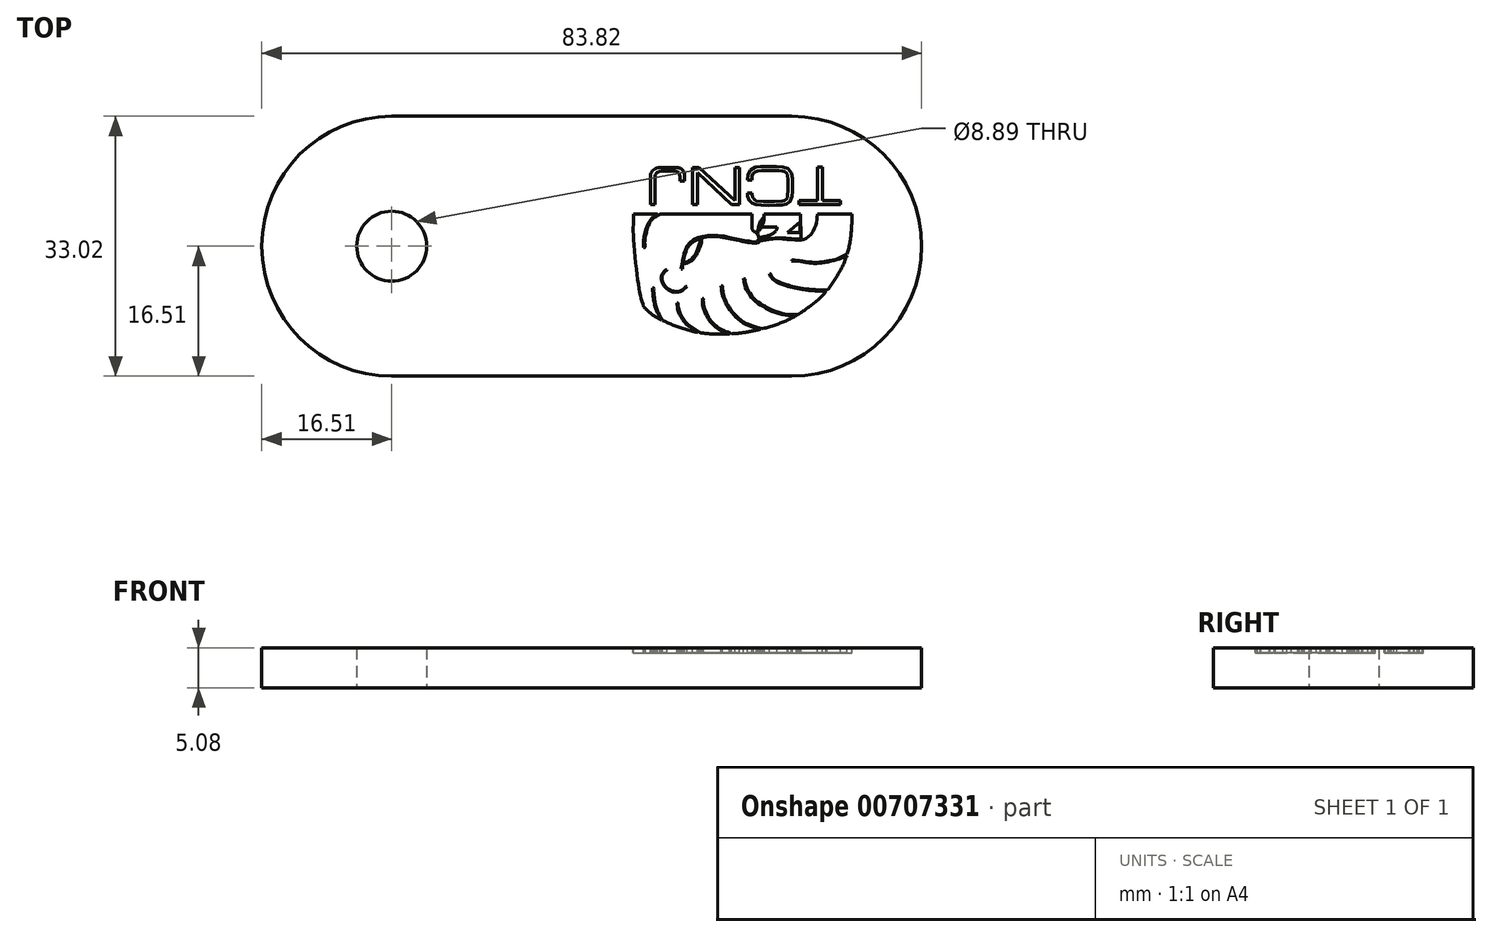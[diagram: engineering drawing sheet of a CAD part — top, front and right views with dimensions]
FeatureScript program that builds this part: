
annotation { "Feature Type Name" : "Feature", "Feature Type Description" : "" }
export const myFeature = defineFeature(function(context is Context, id is Id, definition is map)
    precondition{}
    {
        {
            var Q0;
            Q0=qCreatedBy(makeId("Top.planeOp"),FACE);
            var sketch = newSketch(context, id + "F0", { "sketchPlane" : qUnion([Q0])});
            skLineSegment(sketch, "E0.bottom", {"start": v(0, 0) * mm, "end": v(-50.8, 0) * mm});
            skLineSegment(sketch, "E0.top", {"start": v(0, 33.02) * mm, "end": v(-50.8, 33.02) * mm});
            skArc(sketch, "E1", {"start": v(0, 0) * mm, "mid": v(16.51, 16.51) * mm, "end": v(0, 33.02) * mm});
            skArc(sketch, "E2", {"start": v(-50.8, 33.02) * mm, "mid": v(-67.31, 16.5) * mm, "end": v(-50.8, 0) * mm});
            skCircle(sketch, "E3", {"center": v(-50.8, 16.5) * mm, "radius": 4.45 * mm});
            skSolve(sketch);
        }
        {
            var Q0;
            Q0=makeQuery(id+"F0.imprint","IMPRINT",FACE,{"disambiguationData":[TD([[makeQuery(id+"F0.imprint","IMPRINT",EDGE,{"derivedFrom":sQuery(id+"F0.wireOp",EDGE,"E0.bottom")}),-1.0]])]});
            extrude(context, id + "F1", {"entities" : qUnion([Q0]), "depth" : 5.08 * mm, "offsetDistance" : 25.4 * mm});
        }
        {
            var Q0;
            Q0=makeQuery(id+"F1.opExtrude","CAP_FACE",FACE,{"disambiguationData":[OSD([sQuery(id+"F0.wireOp",EDGE,"E0.bottom"),sQuery(id+"F0.wireOp",EDGE,"E0.top"),sQuery(id+"F0.wireOp",EDGE,"E1"),sQuery(id+"F0.wireOp",EDGE,"E2"),sQuery(id+"F0.wireOp",EDGE,"E3")])],"isStart":false});
            var sketch = newSketch(context, id + "F2", { "sketchPlane" : qUnion([Q0])});
            skLineSegment(sketch, "E4", {"start": v(-20.1, 20.57) * mm, "end": v(7.7, 20.57) * mm});
            skFitSpline(sketch, "E5", {"points": [v(-20.1, 20.57) * mm, v(-20.1, 19.6) * mm, v(-20.1, 17.78) * mm, v(-19.6, 12.72) * mm, v(-19.17, 10.09) * mm, v(-18.79, 8.8) * mm], "startDerivative": vector(0.07, -7.05) * mm, "endDerivative": vector(2.6, -7.75) * mm});
            skFitSpline(sketch, "E6", {"points": [v(-18.79, 8.8) * mm, v(-17.66, 7.8) * mm, v(-16.06, 6.93) * mm, v(-14.16, 6.16) * mm, v(-11.87, 5.55) * mm, v(-9.58, 5.34) * mm, v(-7, 5.42) * mm, v(-4.4, 5.85) * mm, v(-1.6, 6.68) * mm, v(0.61, 7.71) * mm, v(2.2, 8.8) * mm, v(4.02, 10.35) * mm, v(5.62, 12.5) * mm, v(6.75, 14.62) * mm, v(7.44, 17.17) * mm, v(7.7, 20.57) * mm], "startDerivative": vector(19.8, -19.68) * mm, "endDerivative": vector(1.84, 44) * mm});
            skFitSpline(sketch, "E7", {"points": [v(-18.79, 16.33) * mm, v(-18.79, 17.43) * mm, v(-18.52, 18.6) * mm, v(-18.03, 19.74) * mm, v(-17.58, 20.25) * mm, v(-17.3, 20.4) * mm, v(-17.03, 20.57) * mm], "startDerivative": vector(-0.28, 5.46) * mm, "endDerivative": vector(2.48, 1.54) * mm});
            skFitSpline(sketch, "E8", {"points": [v(-15.86, 13.57) * mm, v(-16.17, 13.35) * mm, v(-16.41, 13.03) * mm, v(-16.55, 12.68) * mm, v(-16.53, 12.16) * mm, v(-16.33, 11.62) * mm, v(-15.95, 11.17) * mm, v(-15.56, 10.88) * mm, v(-15.1, 10.67) * mm, v(-14.57, 10.67) * mm, v(-14.03, 10.8) * mm, v(-13.6, 11.1) * mm, v(-13.31, 11.36) * mm], "startDerivative": vector(-4.42, -2.67) * mm, "endDerivative": vector(3.59, 3.47) * mm});
            skFitSpline(sketch, "E9", {"points": [v(-13.88, 13.59) * mm, v(-13.76, 14.6) * mm, v(-13.51, 15.6) * mm, v(-13.15, 16.46) * mm, v(-12.34, 17.17) * mm, v(-11.66, 17.48) * mm, v(-10.7, 17.69) * mm, v(-9.36, 17.7) * mm, v(-8.1, 17.5) * mm, v(-6.87, 17.26) * mm, v(-5.5, 16.98) * mm, v(-4.76, 16.92) * mm, v(-4.16, 17.05) * mm, v(-4, 17.61) * mm, v(-4.26, 18.32) * mm], "startDerivative": vector(1.1, 13.84) * mm, "endDerivative": vector(-5.3, 11.08) * mm});
            skFitSpline(sketch, "E10", {"points": [v(-11.66, 17.48) * mm, v(-11.66, 17) * mm, v(-11.86, 16.36) * mm, v(-12.07, 15.82) * mm, v(-12.34, 15.32) * mm, v(-12.82, 14.8) * mm, v(-13.34, 14.51) * mm, v(-13.79, 14.45) * mm], "startDerivative": vector(0.3, -3.54) * mm, "endDerivative": vector(-3.47, -0.2) * mm});
            skFitSpline(sketch, "E11", {"points": [v(-17.65, 11.2) * mm, v(-17.62, 10.37) * mm, v(-17.45, 9.27) * mm, v(-17.16, 8.36) * mm, v(-16.87, 7.75) * mm, v(-16.53, 7.16) * mm], "startDerivative": vector(0.07, -4.05) * mm, "endDerivative": vector(1.94, -3.3) * mm});
            skFitSpline(sketch, "E12", {"points": [v(-14.57, 9.3) * mm, v(-14.44, 8.4) * mm, v(-14.16, 7.71) * mm, v(-13.44, 6.68) * mm, v(-12.76, 6.16) * mm, v(-11.87, 5.55) * mm], "startDerivative": vector(0.5, -4.93) * mm, "endDerivative": vector(4.36, -3.03) * mm});
            skFitSpline(sketch, "E13", {"points": [v(-7.9, 5.36) * mm, v(-9.17, 5.9) * mm, v(-10.1, 6.68) * mm, v(-10.69, 7.46) * mm, v(-11.2, 8.62) * mm, v(-11.34, 9.88) * mm], "startDerivative": vector(-6.2, 2.18) * mm, "endDerivative": vector(-0.16, 6.21) * mm});
            skFitSpline(sketch, "E14", {"points": [v(-8.94, 11.5) * mm, v(-8.88, 10.72) * mm, v(-8.65, 9.88) * mm, v(-8.2, 8.98) * mm, v(-7.52, 7.97) * mm, v(-6.7, 7.13) * mm, v(-5.58, 6.45) * mm, v(-4.73, 6.16) * mm, v(-3.93, 5.96) * mm], "startDerivative": vector(0.32, -7) * mm, "endDerivative": vector(7.1, -1.6) * mm});
            skFitSpline(sketch, "E15", {"points": [v(-6.13, 12.4) * mm, v(-5.93, 11.44) * mm, v(-5.41, 10.47) * mm, v(-4.77, 9.62) * mm, v(-3.9, 9) * mm, v(-2.76, 8.36) * mm, v(-1.47, 7.9) * mm, v(-0.3, 7.68) * mm, v(0.61, 7.71) * mm], "startDerivative": vector(1.04, -8.34) * mm, "endDerivative": vector(7.87, 0.7) * mm});
            skFitSpline(sketch, "E16", {"points": [v(-2.83, 13.02) * mm, v(-2.66, 12.63) * mm, v(-2.11, 12.08) * mm, v(-0.46, 11.4) * mm, v(0.61, 11.15) * mm, v(2, 10.92) * mm, v(4.4, 10.76) * mm], "startDerivative": vector(1.32, -3.93) * mm, "endDerivative": vector(10.9, -0.49) * mm});
            skFitSpline(sketch, "E17", {"points": [v(7.01, 15.35) * mm, v(6.04, 14.9) * mm, v(3.9, 14.38) * mm, v(2.2, 14.38) * mm, v(0.61, 14.62) * mm, v(0, 14.62) * mm], "startDerivative": vector(-4.73, -2.58) * mm, "endDerivative": vector(-4.01, -0.27) * mm});
            skFitSpline(sketch, "E18", {"points": [v(3.08, 20.57) * mm, v(3, 19.7) * mm, v(2.84, 19.1) * mm, v(2.47, 18.4) * mm, v(2.03, 17.88) * mm, v(1.53, 17.5) * mm, v(1.06, 17.46) * mm], "startDerivative": vector(-0.33, -4.8) * mm, "endDerivative": vector(-3.39, 0.1) * mm});
            skLineSegment(sketch, "E19", {"start": v(1.06, 17.46) * mm, "end": v(1.06, 20.57) * mm});
            skFitSpline(sketch, "E20", {"points": [v(-4.03, 17.27) * mm, v(-3.65, 17.36) * mm, v(-2.89, 17.46) * mm, v(-2.11, 17.52) * mm, v(-1.29, 17.54) * mm, v(-0.41, 17.49) * mm, v(0.28, 17.42) * mm, v(0.83, 17.4) * mm, v(1.06, 17.46) * mm], "startDerivative": vector(3.45, 0.87) * mm, "endDerivative": vector(2.59, 1.06) * mm});
            skFitSpline(sketch, "E21", {"points": [v(-4.26, 18.32) * mm, v(-4.26, 18.82) * mm, v(-4.16, 19.32) * mm, v(-3.96, 19.74) * mm, v(-3.76, 19.98) * mm, v(-3.52, 20.13) * mm, v(-3.57, 19.58) * mm, v(-3.75, 19.1) * mm, v(-3.9, 18.7) * mm, v(-4.26, 18.32) * mm]});
            skFitSpline(sketch, "E22", {"points": [v(-3.52, 20.13) * mm, v(-3.52, 20.57) * mm], "startDerivative": vector(0, 0.44) * mm, "endDerivative": vector(0, 0.44) * mm});
            skLineSegment(sketch, "E23", {"start": v(-5.06, 20.57) * mm, "end": v(-5.06, 18.82) * mm});
            skFitSpline(sketch, "E24", {"points": [v(-5.06, 18.82) * mm, v(-4.95, 18.52) * mm, v(-4.72, 18.35) * mm, v(-4.5, 18.32) * mm, v(-4.26, 18.32) * mm], "startDerivative": vector(0.3, -1.14) * mm, "endDerivative": vector(1, 0) * mm});
            skLineSegment(sketch, "E25", {"start": v(1.06, 19.6) * mm, "end": v(-0.54, 18.23) * mm});
            skLineSegment(sketch, "E26", {"start": v(-0.54, 18.23) * mm, "end": v(1.06, 18.23) * mm});
            skLineSegment(sketch, "E27", {"start": v(-1.88, 18.94) * mm, "end": v(-3.8, 18.94) * mm});
            skFitSpline(sketch, "E28", {"points": [v(-1.88, 18.94) * mm, v(-1.88, 18.74) * mm, v(-2.1, 18.34) * mm, v(-2.65, 17.96) * mm, v(-3.32, 17.74) * mm, v(-4, 17.61) * mm], "startDerivative": vector(0.2, -1.49) * mm, "endDerivative": vector(-2.97, -0.52) * mm});
            skLineSegment(sketch, "E29", {"start": v(3.28, 26.58) * mm, "end": v(3.28, 22.3) * mm});
            skLineSegment(sketch, "E30", {"start": v(3.28, 22.3) * mm, "end": v(0.93, 22.3) * mm});
            skLineSegment(sketch, "E31", {"start": v(0.93, 22.3) * mm, "end": v(0.93, 21.78) * mm});
            skLineSegment(sketch, "E32", {"start": v(0.93, 21.78) * mm, "end": v(6.22, 21.78) * mm});
            skLineSegment(sketch, "E33", {"start": v(6.22, 21.78) * mm, "end": v(6.22, 22.27) * mm});
            skLineSegment(sketch, "E34", {"start": v(6.22, 22.27) * mm, "end": v(3.9, 22.27) * mm});
            skLineSegment(sketch, "E35", {"start": v(3.9, 22.27) * mm, "end": v(3.9, 26.54) * mm});
            skLineSegment(sketch, "E36", {"start": v(3.9, 26.54) * mm, "end": v(3.28, 26.54) * mm});
            skLineSegment(sketch, "E37", {"start": v(-12.58, 26.56) * mm, "end": v(-12.58, 21.78) * mm});
            skLineSegment(sketch, "E38", {"start": v(-12.58, 21.78) * mm, "end": v(-11.98, 21.78) * mm});
            skLineSegment(sketch, "E39", {"start": v(-11.98, 21.78) * mm, "end": v(-11.98, 25.89) * mm});
            skLineSegment(sketch, "E40", {"start": v(-11.98, 25.89) * mm, "end": v(-7.65, 21.78) * mm});
            skLineSegment(sketch, "E41", {"start": v(-7.65, 21.78) * mm, "end": v(-6.6, 21.78) * mm});
            skLineSegment(sketch, "E42", {"start": v(-6.6, 21.78) * mm, "end": v(-6.6, 26.53) * mm});
            skLineSegment(sketch, "E43", {"start": v(-6.6, 26.53) * mm, "end": v(-7.2, 26.53) * mm});
            skLineSegment(sketch, "E44", {"start": v(-7.2, 26.53) * mm, "end": v(-7.2, 22.3) * mm});
            skLineSegment(sketch, "E45", {"start": v(-7.2, 22.3) * mm, "end": v(-11.77, 26.53) * mm});
            skLineSegment(sketch, "E46", {"start": v(-11.77, 26.53) * mm, "end": v(-12.58, 26.53) * mm});
            skFitSpline(sketch, "E47", {"points": [v(-18.79, 16.33) * mm, v(-18.67, 16.33) * mm, v(-18.66, 16.92) * mm, v(-18.63, 17.36) * mm, v(-18.55, 17.89) * mm, v(-18.42, 18.37) * mm, v(-18.3, 18.81) * mm, v(-18.1, 19.3) * mm, v(-17.9, 19.66) * mm, v(-17.7, 19.96) * mm, v(-17.45, 20.16) * mm, v(-17.18, 20.3) * mm], "startDerivative": vector(2.8, -0.96) * mm, "endDerivative": vector(3.54, 1.71) * mm});
            skFitSpline(sketch, "E48", {"points": [v(-17.18, 20.3) * mm, v(-17, 20.4) * mm, v(-16.7, 20.57) * mm], "startDerivative": vector(0.36, 0.24) * mm, "endDerivative": vector(0.58, 0.29) * mm});
            skFitSpline(sketch, "E49", {"points": [v(-15.86, 13.57) * mm, v(-15.8, 13.5) * mm, v(-15.97, 13.38) * mm, v(-16.14, 13.27) * mm, v(-16.26, 13.11) * mm, v(-16.33, 12.98) * mm, v(-16.41, 12.79) * mm, v(-16.44, 12.67) * mm, v(-16.46, 12.45) * mm, v(-16.45, 12.26) * mm, v(-16.4, 12.07) * mm, v(-16.33, 11.9) * mm, v(-16.26, 11.74) * mm, v(-16.15, 11.59) * mm, v(-16.03, 11.4) * mm, v(-15.86, 11.23) * mm, v(-15.7, 11.1) * mm, v(-15.51, 10.98) * mm, v(-15.33, 10.89) * mm, v(-15.18, 10.81) * mm, v(-15, 10.79) * mm, v(-14.84, 10.75) * mm, v(-14.64, 10.75) * mm, v(-14.37, 10.8) * mm, v(-14.07, 10.89) * mm, v(-13.83, 11.04) * mm, v(-13.56, 11.26) * mm, v(-13.38, 11.4) * mm, v(-13.31, 11.36) * mm], "startDerivative": vector(3.58, -2.7) * mm, "endDerivative": vector(2.81, -3.5) * mm});
            skFitSpline(sketch, "E50", {"points": [v(-17.65, 11.2) * mm, v(-17.52, 11.2) * mm, v(-17.51, 10.94) * mm, v(-17.51, 10.68) * mm, v(-17.5, 10.4) * mm, v(-17.46, 10.11) * mm, v(-17.42, 9.78) * mm, v(-17.39, 9.57) * mm, v(-17.3, 9.16) * mm, v(-17.18, 8.7) * mm, v(-17.03, 8.3) * mm, v(-16.88, 7.97) * mm, v(-16.7, 7.63) * mm, v(-16.4, 7.09) * mm], "startDerivative": vector(3.2, 0.86) * mm, "endDerivative": vector(3.1, -5.4) * mm});
            skFitSpline(sketch, "E51", {"points": [v(-14.57, 9.3) * mm, v(-14.47, 9.3) * mm, v(-14.45, 9.08) * mm, v(-14.4, 8.68) * mm, v(-14.3, 8.38) * mm, v(-14.15, 7.98) * mm, v(-13.99, 7.66) * mm, v(-13.85, 7.4) * mm, v(-13.7, 7.17) * mm, v(-13.48, 6.88) * mm, v(-13.16, 6.58) * mm, v(-12.87, 6.34) * mm, v(-12.54, 6.16) * mm, v(-12.29, 5.96) * mm, v(-11.96, 5.75) * mm, v(-11.64, 5.51) * mm], "startDerivative": vector(3.34, 0.79) * mm, "endDerivative": vector(4.27, -3.28) * mm});
            skFitSpline(sketch, "E52", {"points": [v(-11.34, 9.88) * mm, v(-11.23, 9.88) * mm, v(-11.23, 9.68) * mm, v(-11.2, 9.3) * mm, v(-11.17, 8.96) * mm, v(-11.06, 8.6) * mm, v(-10.95, 8.27) * mm, v(-10.73, 7.8) * mm, v(-10.5, 7.35) * mm, v(-10.17, 6.95) * mm, v(-9.92, 6.67) * mm, v(-9.6, 6.38) * mm, v(-9.33, 6.16) * mm, v(-9.04, 6) * mm, v(-8.6, 5.77) * mm, v(-8.3, 5.66) * mm, v(-7.9, 5.5) * mm, v(-7.62, 5.37) * mm], "startDerivative": vector(4.2, 0.97) * mm, "endDerivative": vector(4.79, -2.44) * mm});
            skFitSpline(sketch, "E53", {"points": [v(-8.94, 11.5) * mm, v(-8.8, 11.5) * mm, v(-8.78, 11.21) * mm, v(-8.76, 10.91) * mm, v(-8.68, 10.5) * mm, v(-8.58, 10.08) * mm, v(-8.4, 9.59) * mm, v(-8.21, 9.21) * mm, v(-8.06, 8.98) * mm, v(-7.82, 8.64) * mm, v(-7.54, 8.2) * mm, v(-7.27, 7.89) * mm, v(-6.97, 7.57) * mm, v(-6.7, 7.35) * mm, v(-6.46, 7.13) * mm, v(-6.14, 6.89) * mm, v(-5.83, 6.7) * mm, v(-5.54, 6.58) * mm, v(-5.18, 6.45) * mm, v(-4.75, 6.3) * mm, v(-4.23, 6.16) * mm, v(-3.68, 6.03) * mm], "startDerivative": vector(5.84, 1.58) * mm, "endDerivative": vector(9.59, -2.08) * mm});
            skFitSpline(sketch, "E54", {"points": [v(-6.13, 12.4) * mm, v(-5.98, 12.4) * mm, v(-5.93, 12.12) * mm, v(-5.87, 11.74) * mm, v(-5.77, 11.4) * mm, v(-5.58, 10.98) * mm, v(-5.42, 10.75) * mm, v(-5.2, 10.4) * mm, v(-4.92, 10.04) * mm, v(-4.62, 9.7) * mm, v(-4.34, 9.47) * mm, v(-4.1, 9.3) * mm, v(-3.81, 9.13) * mm, v(-3.54, 8.98) * mm, v(-3.23, 8.79) * mm, v(-2.8, 8.56) * mm, v(-2.22, 8.3) * mm, v(-1.71, 8.14) * mm, v(-1.2, 7.97) * mm, v(-0.63, 7.86) * mm, v(-0.13, 7.8) * mm, v(0.39, 7.8) * mm, v(0.85, 7.86) * mm], "startDerivative": vector(6.22, 1.59) * mm, "endDerivative": vector(9.33, 1.35) * mm});
            skFitSpline(sketch, "E55", {"points": [v(-2.83, 13.02) * mm, v(-2.68, 13.02) * mm, v(-2.62, 12.83) * mm, v(-2.51, 12.6) * mm, v(-2.32, 12.4) * mm, v(-2.1, 12.23) * mm, v(-1.71, 12.05) * mm, v(-1.4, 11.87) * mm, v(-1.02, 11.71) * mm, v(-0.56, 11.58) * mm, v(-0.26, 11.5) * mm, v(0, 11.39) * mm, v(0.32, 11.33) * mm, v(0.74, 11.26) * mm, v(1.22, 11.18) * mm, v(1.78, 11.09) * mm, v(2.24, 11.03) * mm, v(2.78, 11) * mm, v(3.46, 10.95) * mm, v(4.52, 10.91) * mm], "startDerivative": vector(5.25, 1.24) * mm, "endDerivative": vector(12.95, -0.29) * mm});
            skFitSpline(sketch, "E56", {"points": [v(0, 14.62) * mm, v(0, 14.74) * mm, v(0.4, 14.74) * mm, v(0.8, 14.7) * mm, v(1.39, 14.62) * mm, v(1.85, 14.54) * mm, v(2.2, 14.48) * mm, v(2.75, 14.46) * mm, v(3.33, 14.46) * mm, v(3.75, 14.48) * mm, v(4.12, 14.54) * mm, v(4.53, 14.62) * mm, v(5.23, 14.75) * mm, v(5.75, 14.9) * mm, v(6.11, 15.04) * mm, v(6.43, 15.2) * mm, v(7.06, 15.49) * mm], "startDerivative": vector(-1.3, 4.24) * mm, "endDerivative": vector(8.66, 4.12) * mm});
            skFitSpline(sketch, "E57", {"points": [v(-13.88, 13.59) * mm, v(-14.02, 13.59) * mm], "startDerivative": vector(-0.15, 0) * mm, "endDerivative": vector(-0.15, 0) * mm});
            skFitSpline(sketch, "E58", {"points": [v(-14.02, 13.59) * mm, v(-13.93, 14.15) * mm, v(-13.88, 14.62) * mm, v(-13.78, 15.05) * mm, v(-13.7, 15.3) * mm, v(-13.64, 15.6) * mm, v(-13.5, 16) * mm, v(-13.34, 16.46) * mm, v(-12.98, 16.87) * mm, v(-12.53, 17.26) * mm, v(-11.98, 17.55) * mm, v(-11.42, 17.7) * mm, v(-10.66, 17.84) * mm, v(-10.07, 17.87) * mm, v(-9.36, 17.88) * mm, v(-8.25, 17.7) * mm, v(-7.62, 17.57) * mm, v(-6.9, 17.44) * mm, v(-6.3, 17.3) * mm, v(-5.63, 17.17) * mm, v(-5.07, 17.06) * mm, v(-4.62, 17.05) * mm, v(-4.25, 17.17) * mm, v(-4.16, 17.52) * mm, v(-4.25, 17.96) * mm, v(-4.77, 18.19) * mm, v(-5.03, 18.41) * mm, v(-5.2, 18.73) * mm, v(-5.22, 20.57) * mm], "startDerivative": vector(3.34, 17.21) * mm, "endDerivative": vector(0.1, 18.52) * mm});
            skFitSpline(sketch, "E59", {"points": [v(-13.8, 14.32) * mm, v(-13.31, 14.33) * mm, v(-12.8, 14.6) * mm, v(-12.4, 15) * mm, v(-12.06, 15.46) * mm, v(-11.74, 16.12) * mm, v(-11.48, 16.96) * mm, v(-11.47, 17.53) * mm], "startDerivative": vector(3.83, -0.3) * mm, "endDerivative": vector(-0.22, 3.97) * mm});
            skFitSpline(sketch, "E60", {"points": [v(-4.03, 17.17) * mm, v(-3.54, 17.27) * mm, v(-3.26, 17.3) * mm, v(-1.7, 17.46) * mm, v(0.13, 17.3) * mm, v(1.14, 17.3) * mm, v(1.74, 17.46) * mm, v(2.47, 18.05) * mm, v(3.04, 19.1) * mm, v(3.22, 19.83) * mm, v(3.26, 20.57) * mm], "startDerivative": vector(7.33, 1.75) * mm, "endDerivative": vector(0.14, 8.2) * mm});
            skFitSpline(sketch, "E61", {"points": [v(1.15, 20.57) * mm, v(1.22, 17.45) * mm], "startDerivative": vector(0.07, -3.11) * mm, "endDerivative": vector(0.07, -3.11) * mm});
            skFitSpline(sketch, "E62", {"points": [v(-4.25, 17.96) * mm, v(-4.5, 18.32) * mm], "startDerivative": vector(-0.24, 0.36) * mm, "endDerivative": vector(-0.24, 0.36) * mm});
            skFitSpline(sketch, "E63", {"points": [v(-4.26, 18.32) * mm, v(-4.26, 18.53) * mm, v(-4.2, 18.85) * mm, v(-4.16, 19.2) * mm, v(-4.05, 19.47) * mm, v(-3.92, 19.73) * mm, v(-3.75, 19.95) * mm, v(-3.6, 20.08) * mm, v(-3.56, 20.1) * mm, v(-3.52, 20.07) * mm, v(-3.52, 19.94) * mm, v(-3.56, 19.76) * mm, v(-3.61, 19.58) * mm, v(-3.69, 19.32) * mm, v(-3.79, 19.09) * mm, v(-3.87, 18.86) * mm, v(-3.96, 18.69) * mm, v(-4.08, 18.52) * mm, v(-4.16, 18.43) * mm, v(-4.26, 18.37) * mm], "startDerivative": vector(-0.18, 3.68) * mm, "endDerivative": vector(-2.53, -1.43) * mm});
            skFitSpline(sketch, "E64", {"points": [v(-4.26, 18.35) * mm, v(-4.26, 18.35) * mm], "startDerivative": vector(0, 0) * mm, "endDerivative": vector(0, 0) * mm});
            skFitSpline(sketch, "E65", {"points": [v(-3.5, 20.1) * mm, v(-3.48, 20.57) * mm], "startDerivative": vector(0.02, 0.47) * mm, "endDerivative": vector(0.02, 0.47) * mm});
            skFitSpline(sketch, "E66", {"points": [v(0.95, 17.38) * mm, v(0.95, 17.37) * mm], "startDerivative": vector(0, 0) * mm, "endDerivative": vector(0, 0) * mm});
            skFitSpline(sketch, "E67", {"points": [v(-4.03, 17.17) * mm, v(-4.08, 17.16) * mm], "startDerivative": vector(-0.05, 0) * mm, "endDerivative": vector(-0.05, 0) * mm});
            skFitSpline(sketch, "E68", {"points": [v(-4.26, 18.37) * mm, v(-4.26, 18.37) * mm], "startDerivative": vector(0, 0) * mm, "endDerivative": vector(0, 0) * mm});
            skSolve(sketch);
        }
        {
            var Q0;
            {var subQ5=sQuery(id+"F2.wireOp",EDGE,"E5");Q0=makeQuery(id+"F2.imprint","IMPRINT",FACE,{"disambiguationData":[TD([[makeQuery(id+"F2.imprint","IMPRINT",EDGE,{"derivedFrom":subQ5}),1.0]])]});}
            var sketch = newSketch(context, id + "F3", { "sketchPlane" : qUnion([Q0])});
            skFitSpline(sketch, "E69", {"points": [v(-5.05, 24.97) * mm, v(-5, 25.44) * mm, v(-4.9, 25.71) * mm, v(-4.69, 25.92) * mm, v(-4.39, 26.05) * mm, v(-4.09, 26.08) * mm, v(-1.4, 26.1) * mm, v(-1.15, 26.07) * mm, v(-0.94, 26.01) * mm, v(-0.74, 25.9) * mm, v(-0.6, 25.72) * mm, v(-0.53, 25.49) * mm, v(-0.49, 23) * mm, v(-0.51, 22.83) * mm, v(-0.56, 22.65) * mm, v(-0.65, 22.5) * mm, v(-0.81, 22.34) * mm, v(-0.98, 22.27) * mm, v(-1.12, 22.22) * mm, v(-4.38, 22.22) * mm, v(-4.58, 22.32) * mm, v(-4.72, 22.42) * mm, v(-4.84, 22.57) * mm], "startDerivative": vector(0.84, 10.23) * mm, "endDerivative": vector(-3.41, 5.34) * mm});
            skFitSpline(sketch, "E70", {"points": [v(-4.84, 22.57) * mm, v(-4.96, 22.76) * mm, v(-5, 23) * mm, v(-5.01, 23.26) * mm], "startDerivative": vector(-0.42, 0.55) * mm, "endDerivative": vector(0, 0.73) * mm});
            skLineSegment(sketch, "E71", {"start": v(-5.01, 23.26) * mm, "end": v(-5.58, 23.26) * mm});
            skLineSegment(sketch, "E72", {"start": v(-5.58, 23.26) * mm, "end": v(-5.58, 22.87) * mm});
            skFitSpline(sketch, "E73", {"points": [v(-5.58, 22.87) * mm, v(-5.52, 22.57) * mm, v(-5.41, 22.35) * mm, v(-5.26, 22.15) * mm, v(-4.99, 21.96) * mm, v(-4.78, 21.85) * mm, v(-4.42, 21.77) * mm, v(-3.92, 21.71) * mm, v(-3.14, 21.7) * mm, v(-2.33, 21.7) * mm, v(-1.45, 21.7) * mm, v(-1.12, 21.75) * mm, v(-0.79, 21.82) * mm, v(-0.48, 21.96) * mm, v(-0.22, 22.18) * mm, v(0, 22.53) * mm, v(0.09, 23) * mm, v(0.1, 23.52) * mm, v(0.09, 24.06) * mm, v(0.1, 24.79) * mm, v(0.09, 25.32) * mm, v(0, 25.78) * mm, v(-0.3, 26.21) * mm, v(-0.63, 26.45) * mm, v(-1.1, 26.57) * mm, v(-1.76, 26.6) * mm, v(-2.74, 26.6) * mm, v(-3.8, 26.6) * mm, v(-4.34, 26.6) * mm, v(-4.77, 26.49) * mm, v(-5.2, 26.23) * mm, v(-5.44, 25.87) * mm, v(-5.58, 25.47) * mm, v(-5.58, 24.9) * mm], "startDerivative": vector(1.53, -13.15) * mm, "endDerivative": vector(1.22, -17.98) * mm});
            skLineSegment(sketch, "E74", {"start": v(-5.58, 24.9) * mm, "end": v(-5.05, 24.9) * mm});
            skLineSegment(sketch, "E75", {"start": v(-5.05, 24.9) * mm, "end": v(-5.05, 24.97) * mm});
            skLineSegment(sketch, "E76", {"start": v(-17.34, 25.48) * mm, "end": v(-17.34, 21.79) * mm});
            skLineSegment(sketch, "E77", {"start": v(-17.34, 21.79) * mm, "end": v(-17.9, 21.79) * mm});
            skLineSegment(sketch, "E78", {"start": v(-17.9, 21.79) * mm, "end": v(-17.9, 25.45) * mm});
            skFitSpline(sketch, "E79", {"points": [v(-17.34, 25.48) * mm, v(-17.23, 25.7) * mm, v(-17.12, 25.82) * mm, v(-16.95, 25.94) * mm, v(-16.86, 26) * mm, v(-14.64, 26.02) * mm, v(-14.45, 25.97) * mm, v(-14.32, 25.85) * mm, v(-14.22, 25.65) * mm, v(-14.2, 25.48) * mm, v(-14.15, 24.8) * mm], "startDerivative": vector(1.4, 2.66) * mm, "endDerivative": vector(0.5, -5.6) * mm});
            skFitSpline(sketch, "E80", {"points": [v(-17.9, 25.45) * mm, v(-17.9, 25.69) * mm, v(-17.81, 25.88) * mm, v(-17.7, 26.07) * mm, v(-17.57, 26.2) * mm, v(-17.34, 26.35) * mm, v(-17.16, 26.44) * mm, v(-17.01, 26.47) * mm, v(-14.57, 26.51) * mm, v(-14.38, 26.48) * mm, v(-14.19, 26.44) * mm, v(-14.02, 26.35) * mm, v(-13.84, 26.2) * mm, v(-13.74, 26.07) * mm, v(-13.66, 25.87) * mm, v(-13.63, 25.65) * mm, v(-13.62, 25.45) * mm, v(-13.6, 25.07) * mm, v(-13.58, 24.8) * mm], "startDerivative": vector(-0.48, 4.86) * mm, "endDerivative": vector(0.36, -4.58) * mm});
            skFitSpline(sketch, "E81", {"points": [v(-14.15, 24.8) * mm, v(-13.58, 24.8) * mm], "startDerivative": vector(0.57, 0) * mm, "endDerivative": vector(0.57, 0) * mm});
            skSolve(sketch);
        }
        {
            var Q0;
            {var subQ0=sQuery(id+"F2.wireOp",EDGE,"E30");Q0=makeQuery(id+"F2.imprint","IMPRINT",FACE,{"disambiguationData":[TD([[makeQuery(id+"F2.imprint","IMPRINT",EDGE,{"derivedFrom":subQ0}),1.0]])]});}
            var Q1;
            {var subQ0=sQuery(id+"F2.wireOp",EDGE,"E38");Q1=makeQuery(id+"F2.imprint","IMPRINT",FACE,{"disambiguationData":[TD([[makeQuery(id+"F2.imprint","IMPRINT",EDGE,{"derivedFrom":subQ0}),1.0]])]});}
            var Q2;
            {var subQ0=sQuery(id+"F2.wireOp",EDGE,"E22");Q2=makeQuery(id+"F2.imprint","IMPRINT",FACE,{"disambiguationData":[TD([[makeQuery(id+"F2.imprint","IMPRINT",EDGE,{"derivedFrom":subQ0}),-1.0]])]});}
            var Q3;
            {var subQ24=sQuery(id+"F2.wireOp",EDGE,"E5");Q3=makeQuery(id+"F2.imprint","IMPRINT",FACE,{"disambiguationData":[TD([[makeQuery(id+"F2.imprint","IMPRINT",EDGE,{"derivedFrom":subQ24}),1.0]])]});}
            var Q4;
            {var subQ0=sQuery(id+"F2.wireOp",EDGE,"E10");Q4=makeQuery(id+"F2.imprint","IMPRINT",FACE,{"disambiguationData":[TD([[makeQuery(id+"F2.imprint","IMPRINT",EDGE,{"derivedFrom":subQ0}),-1.0]])]});}
            var Q5;
            {var subQ0=sQuery(id+"F2.wireOp",EDGE,"E19");var subQ7=sQuery(id+"F2.wireOp",EDGE,"E4");var subQ8=makeQuery(id+"F2.imprint","INTERSECT",VERTEX,{"derivedFrom":[subQ7,subQ0]});Q5=makeQuery(id+"F2.imprint","IMPRINT",FACE,{"disambiguationData":[TD([[makeQuery(id+"F2.imprint","IMPRINT",EDGE,{"disambiguationData":[TD([[subQ8,-1.0]])],"derivedFrom":subQ7}),-1.0]])]});}
            var Q6;
            {var subQ5=sQuery(id+"F2.wireOp",EDGE,"E23");Q6=makeQuery(id+"F2.imprint","IMPRINT",FACE,{"disambiguationData":[TD([[makeQuery(id+"F2.imprint","IMPRINT",EDGE,{"derivedFrom":subQ5}),-1.0]])]});}
            var Q7;
            {var subQ7=sQuery(id+"F2.wireOp",EDGE,"E20");Q7=makeQuery(id+"F2.imprint","IMPRINT",FACE,{"disambiguationData":[TD([[makeQuery(id+"F2.imprint","IMPRINT",EDGE,{"derivedFrom":subQ7}),1.0]])]});}
            var Q8;
            {var subQ0=sQuery(id+"F2.wireOp",EDGE,"E68");Q8=makeQuery(id+"F2.imprint","IMPRINT",FACE,{"disambiguationData":[TD([[makeQuery(id+"F2.imprint","IMPRINT",EDGE,{"derivedFrom":subQ0}),-1.0]])]});}
            extrude(context, id + "F4", {"entities" : qUnion([Q0, Q1, Q2, Q3, Q4, Q5, Q6, Q7, Q8]), "operationType" : NewBodyOperationType.REMOVE, "oppositeDirection" : true, "depth" : 0.64 * mm, "offsetDistance" : 25.4 * mm});
        }
        {
            var Q0;
            Q0 = qSketchRegion(id + "F3", true);
            extrude(context, id + "F5", {"entities" : qUnion([Q0]), "operationType" : NewBodyOperationType.REMOVE, "oppositeDirection" : true, "depth" : 0.64 * mm, "offsetDistance" : 25.4 * mm});
        }
    });
